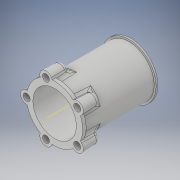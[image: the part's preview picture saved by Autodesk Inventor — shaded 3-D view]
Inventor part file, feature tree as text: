
AUTODESK INVENTOR PART (.ipt)
format: ipt  version: 2018 (Build 220112000, 112)  size: 520,192 bytes
history: native  units: in
note: dims shown in document units (in); Inventor stores cm internally (conversion verified against a paired STEP export)
features: sketch x7, extrude x6, fillet x2, pattern_circular x2, draft x1, other x1
ambient origin geometry x8: Origin, YZ Plane, XZ Plane, XY Plane, X Axis, Y Axis, Z Axis, Center Point
bodies: Solid1 (feature_tree)
feature tree (19):
  extrude  "Extrusion1"  Depth=5.6693in
  extrude  "Extrusion2"  Depth=6.2992in
  extrude  "Extrusion3"  Depth=0.3937in
  sketch  "Sketch6"  dims[d8=0.1969in d9=0.0in d11=0.2474in]
  extrude  "Extrusion4"  Depth=0.2474in
  extrude  "Extrusion5"  Depth=3.1496in
  draft  "FaceDraft1"
  fillet  "Fillet1"  Radius=3.1496in
  fillet  "Fillet2"  Radius=1.9685in
  other  "Work Axis1"
  pattern_circular  "Circular Pattern1"  [2 undecoded]
  extrude  "Extrusion6"  Depth=0.4724in
  pattern_circular  "Circular Pattern2"  Count=5 Angle=360.0deg
  sketch  "Sketch9"  dims[d19=0.0172in d20=0.4724in d21=0.4724in d22=1.9685in d23=360.0deg d25=1.5748in d26=0.0in d27=1.9685in d28=360.0deg]
  sketch  "Sketch1"  dims[d0=4.8819in d1=5.6693in]
  sketch  "Sketch2"  dims[d2=8.563in d3=0.0in d4=6.2992in]
  sketch  "Sketch3"  dims[d5=0.3937in d6=0.0in d7=6.1024in]
  sketch  "Sketch7"  dims[d12=0.7874in d13=1.378in d14=3.1496in d15=1.9685in d16=0.0in]
  sketch  "Sketch8"  dims[d17=0.1969in d18=0.0in]
note: 2 required parameter values undecoded (feature->parameter linkage not recoverable at this tier; creation-order binding heuristic only, values carry confidence <= 0.55)
